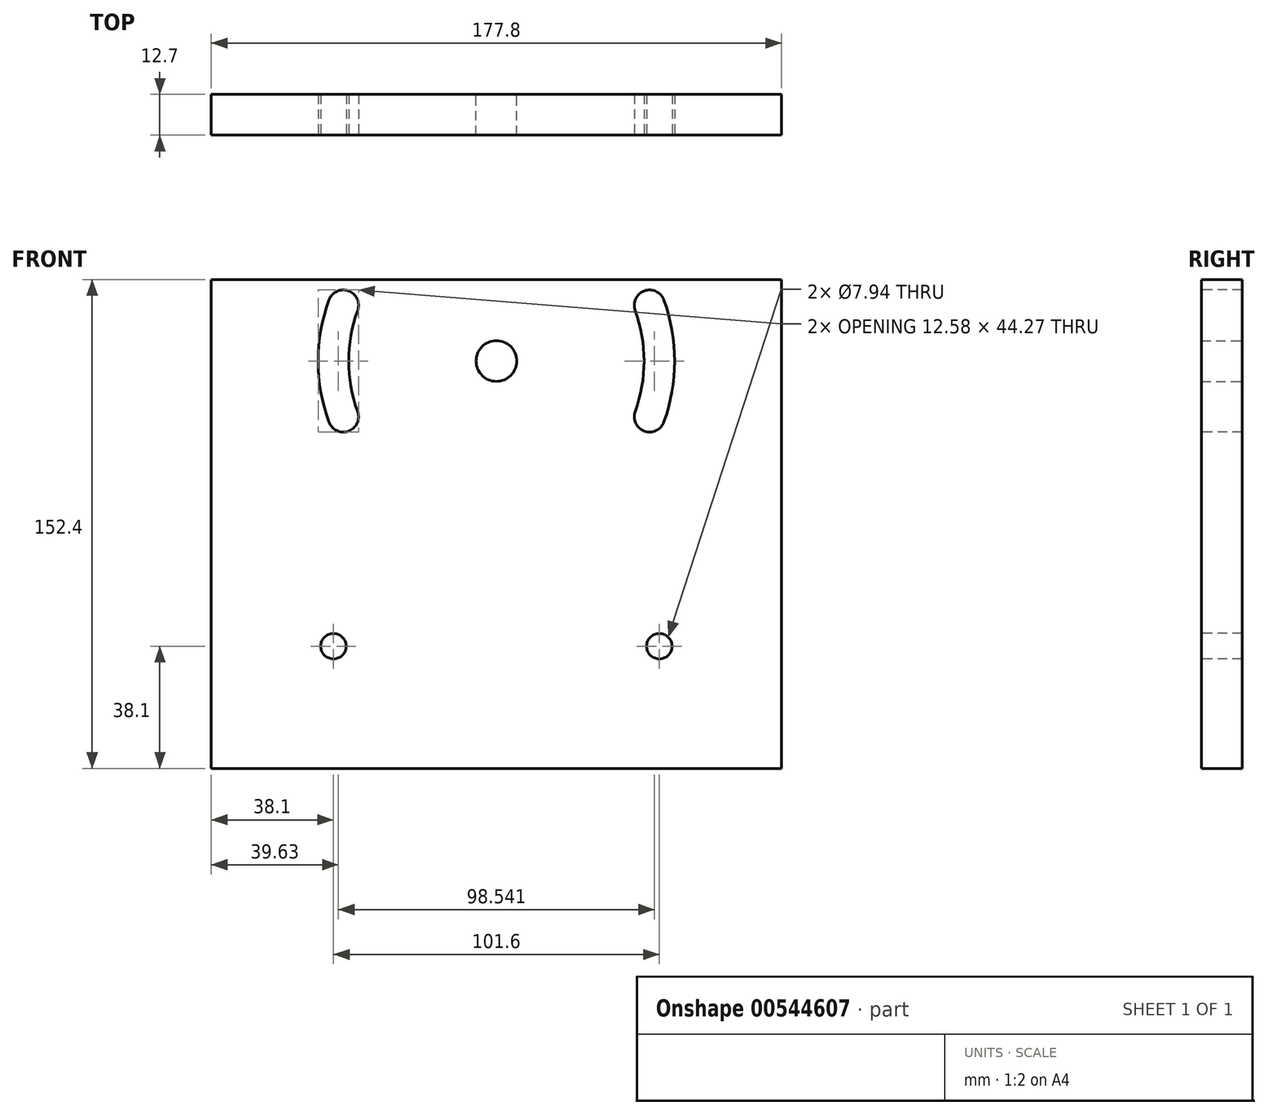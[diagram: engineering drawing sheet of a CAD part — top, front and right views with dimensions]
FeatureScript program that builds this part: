
annotation { "Feature Type Name" : "Feature", "Feature Type Description" : "" }
export const myFeature = defineFeature(function(context is Context, id is Id, definition is map)
    precondition{}
    {
        {
            var Q0;
            Q0=qCreatedBy(makeId("Front.planeOp"),FACE);
            var sketch = newSketch(context, id + "F0", { "sketchPlane" : qUnion([Q0])});
            skCircle(sketch, "E0", {"center": v(0, 0) * mm, "radius": 6.35 * mm});
            skLineSegment(sketch, "E1.bottom", {"start": v(-95.25, -127) * mm, "end": v(88.9, -127) * mm});
            skLineSegment(sketch, "E1.top", {"start": v(-95.25, 25.4) * mm, "end": v(88.9, 25.4) * mm});
            skLineSegment(sketch, "E1.left", {"start": v(-95.25, -127) * mm, "end": v(-95.25, 25.4) * mm});
            skLineSegment(sketch, "E1.right", {"start": v(88.9, -127) * mm, "end": v(88.9, 25.4) * mm});
            skSolve(sketch);
        }
        {
            var Q0;
            Q0 = qSketchRegion(id + "F0", true);
            extrude(context, id + "F1", {"entities" : qUnion([Q0]), "depth" : 12.7 * mm, "offsetDistance" : 25.4 * mm});
        }
        {
            var Q0;
            Q0=makeQuery(id+"F1.opExtrude","CAP_FACE",FACE,{"disambiguationData":[OSD([sQuery(id+"F0.wireOp",EDGE,"E0"),sQuery(id+"F0.wireOp",EDGE,"E1.bottom"),sQuery(id+"F0.wireOp",EDGE,"E1.top"),sQuery(id+"F0.wireOp",EDGE,"E1.left"),sQuery(id+"F0.wireOp",EDGE,"E1.right")])],"isStart":false});
            var sketch = newSketch(context, id + "F2", { "sketchPlane" : qUnion([Q0])});
            skCircle(sketch, "E2", {"center": v(0, 0) * mm, "radius": 50.8 * mm, "construction": true});
            skArc(sketch, "E3", {"start": v(52.21, 19) * mm, "mid": v(46.1, 21.85) * mm, "end": v(43.26, 15.75) * mm});
            skArc(sketch, "E4", {"start": v(43.26, -15.75) * mm, "mid": v(46.1, -21.85) * mm, "end": v(52.21, -19) * mm});
            skLineSegment(sketch, "E5", {"start": v(0, 0) * mm, "end": v(47.74, 17.37) * mm, "construction": true});
            skLineSegment(sketch, "E6", {"start": v(0, 0) * mm, "end": v(50.8, 0) * mm, "construction": true});
            skLineSegment(sketch, "E7", {"start": v(0, 0) * mm, "end": v(47.74, -17.37) * mm, "construction": true});
            skArc(sketch, "E8", {"start": v(43.26, -15.75) * mm, "mid": v(46.04, 0) * mm, "end": v(43.26, 15.75) * mm});
            skArc(sketch, "E9", {"start": v(52.21, -19) * mm, "mid": v(55.56, 0) * mm, "end": v(52.21, 19) * mm});
            skSolve(sketch);
        }
        {
            var Q0;
            Q0 = qSketchRegion(id + "F2", true);
            extrude(context, id + "F3", {"entities" : qUnion([Q0]), "operationType" : NewBodyOperationType.REMOVE, "endBound" : BoundingType.THROUGH_ALL, "oppositeDirection" : true, "depth" : 25.4 * mm, "offsetDistance" : 25.4 * mm});
        }
        {
            var Q0;
            Q0=makeQuery(id+"F1.opExtrude","SWEPT_BODY",BODY,{"disambiguationData":[OSD([sQuery(id+"F0.wireOp",EDGE,"E0"),sQuery(id+"F0.wireOp",EDGE,"E1.bottom"),sQuery(id+"F0.wireOp",EDGE,"E1.top"),sQuery(id+"F0.wireOp",EDGE,"E1.left"),sQuery(id+"F0.wireOp",EDGE,"E1.right")])]});
            var Q1;
            Q1=qCreatedBy(makeId("Right.planeOp"),FACE);
            mirror(context, id + "F4", {"operationType" : NewBodyOperationType.INTERSECT, "entities" : qUnion([Q0]), "mirrorPlane" : qUnion([Q1])});
        }
        {
            var Q0;
            Q0=makeQuery(id+"F1.opExtrude","CAP_FACE",FACE,{"disambiguationData":[OSD([sQuery(id+"F0.wireOp",EDGE,"E0"),sQuery(id+"F0.wireOp",EDGE,"E1.bottom"),sQuery(id+"F0.wireOp",EDGE,"E1.top"),sQuery(id+"F0.wireOp",EDGE,"E1.left"),sQuery(id+"F0.wireOp",EDGE,"E1.right")])],"isStart":false});
            var sketch = newSketch(context, id + "F5", { "sketchPlane" : qUnion([Q0])});
            skPoint(sketch, "E10", {"position": v(50.8, -88.9) * mm});
            skPoint(sketch, "E11", {"position": v(-50.8, -88.9) * mm});
            skSolve(sketch);
        }
        {
            var Q0;
            Q0=sQuery(id+"F5.wireOp",VERTEX,"E10");
            var Q1;
            Q1=sQuery(id+"F5.wireOp",VERTEX,"E11");
            var Q2;
            Q2=makeQuery(id+"F1.opExtrude","SWEPT_BODY",BODY,{"disambiguationData":[OSD([sQuery(id+"F0.wireOp",EDGE,"E0"),sQuery(id+"F0.wireOp",EDGE,"E1.bottom"),sQuery(id+"F0.wireOp",EDGE,"E1.top"),sQuery(id+"F0.wireOp",EDGE,"E1.left"),sQuery(id+"F0.wireOp",EDGE,"E1.right")])]});
            hole(context, id + "F6", {"style" : HoleStyle.SIMPLE, "endStyle" : HoleEndStyle.THROUGH, "holeDiameter" : 7.94 * mm, "majorDiameter" : 6.35 * mm, "isTappedThrough" : true, "tappedDepth" : 12.7 * mm, "tapClearance" : 3, "locations" : qUnion([Q0, Q1]), "scope" : qUnion([Q2])});
        }
        {
            var Q0;
            Q0=qCreatedBy(makeId("Right.planeOp"),FACE);
            cPlane(context, id + "F7", {"entities" : qUnion([Q0]), "cplaneType" : CPlaneType.OFFSET, "offset" : 24.76 * mm, "width" : 152.4 * mm, "height" : 152.4 * mm});
        }
    });
